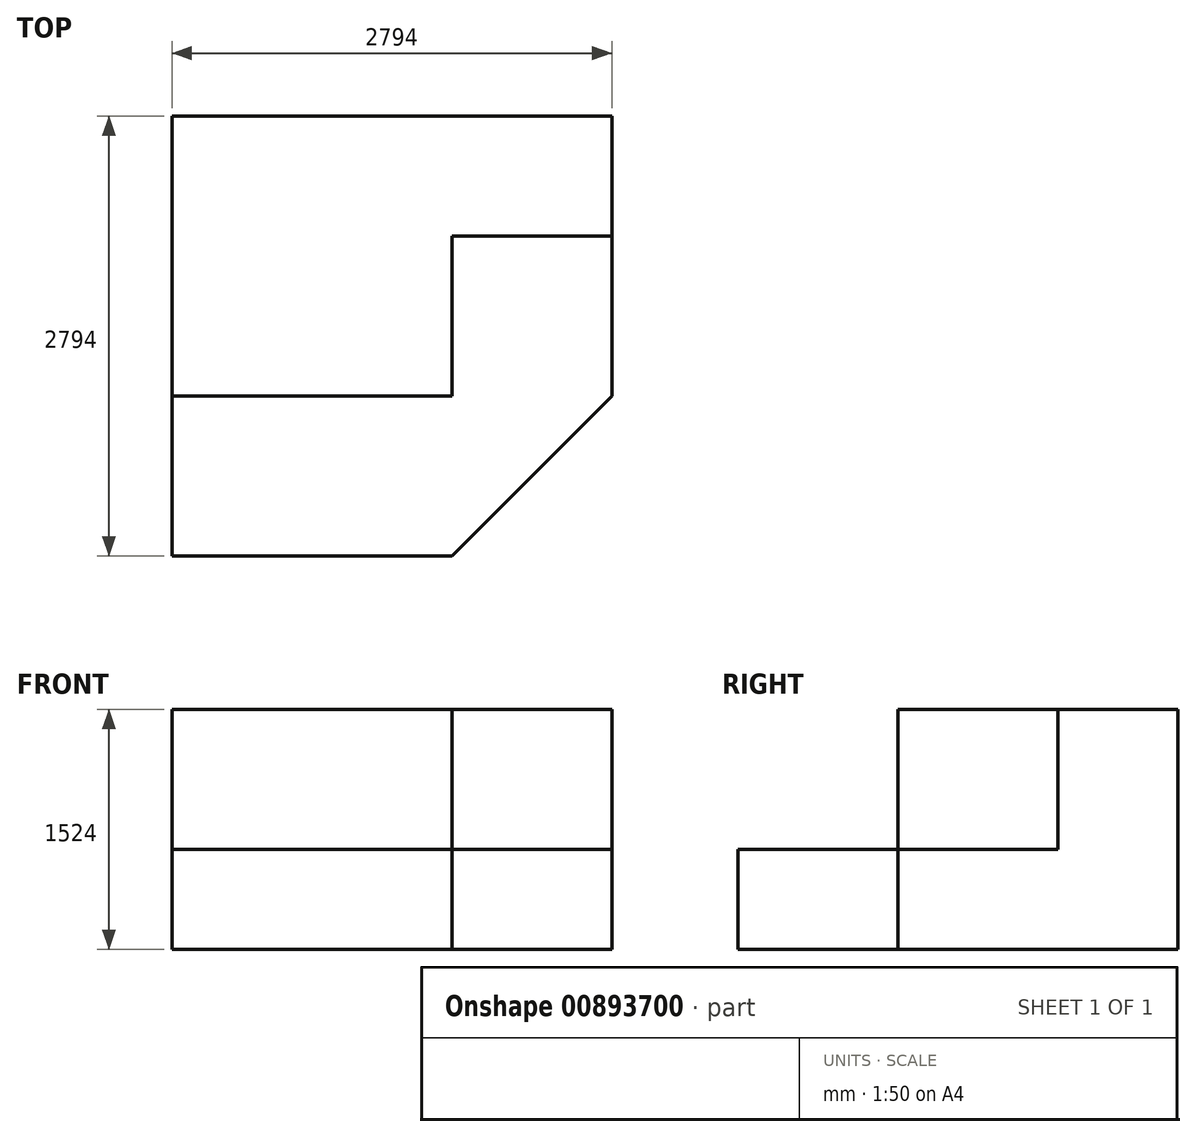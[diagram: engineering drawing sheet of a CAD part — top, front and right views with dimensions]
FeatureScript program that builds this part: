
annotation { "Feature Type Name" : "Feature", "Feature Type Description" : "" }
export const myFeature = defineFeature(function(context is Context, id is Id, definition is map)
    precondition{}
    {
        {
            var Q0;
            Q0=qCreatedBy(makeId("Top.planeOp"),FACE);
            var sketch = newSketch(context, id + "F0", { "sketchPlane" : qUnion([Q0])});
            skLineSegment(sketch, "E0", {"start": v(0, 0) * mm, "end": v(2794, 0) * mm});
            skLineSegment(sketch, "E1", {"start": v(2794, 0) * mm, "end": v(2794, 2794) * mm});
            skLineSegment(sketch, "E2", {"start": v(2794, 2794) * mm, "end": v(0, 2794) * mm});
            skLineSegment(sketch, "E3", {"start": v(0, 2794) * mm, "end": v(0, 0) * mm});
            skSolve(sketch);
        }
        {
            var Q0;
            Q0=makeQuery(id+"F0.imprint","IMPRINT",FACE,{"disambiguationData":[TD([[makeQuery(id+"F0.imprint","IMPRINT",EDGE,{"derivedFrom":sQuery(id+"F0.wireOp",EDGE,"E0")}),1.0]])]});
            extrude(context, id + "F1", {"entities" : qUnion([Q0]), "depth" : 635 * mm, "offsetDistance" : 25.4 * mm});
        }
        {
            var Q0;
            Q0=makeQuery(id+"F1.opExtrude","CAP_FACE",FACE,{"disambiguationData":[OSD([sQuery(id+"F0.wireOp",EDGE,"E0"),sQuery(id+"F0.wireOp",EDGE,"E1"),sQuery(id+"F0.wireOp",EDGE,"E2"),sQuery(id+"F0.wireOp",EDGE,"E3")])],"isStart":false});
            var sketch = newSketch(context, id + "F2", { "sketchPlane" : qUnion([Q0])});
            skLineSegment(sketch, "E4", {"start": v(0, 2794) * mm, "end": v(2794, 2794) * mm});
            skLineSegment(sketch, "E5", {"start": v(2794, 2794) * mm, "end": v(2794, 2032) * mm});
            skLineSegment(sketch, "E6", {"start": v(2794, 2032) * mm, "end": v(1778, 2032) * mm});
            skLineSegment(sketch, "E7", {"start": v(1778, 2032) * mm, "end": v(1778, 1016) * mm});
            skLineSegment(sketch, "E8", {"start": v(1778, 1016) * mm, "end": v(0, 1016) * mm});
            skLineSegment(sketch, "E9", {"start": v(0, 1016) * mm, "end": v(0, 2794) * mm});
            skSolve(sketch);
        }
        {
            var Q0;
            Q0=makeQuery(id+"F2.imprint","IMPRINT",FACE,{"disambiguationData":[TD([[makeQuery(id+"F2.imprint","IMPRINT",EDGE,{"derivedFrom":sQuery(id+"F2.wireOp",EDGE,"E4")}),1.0]])]});
            extrude(context, id + "F3", {"entities" : qUnion([Q0]), "operationType" : NewBodyOperationType.ADD, "depth" : 889 * mm, "offsetDistance" : 25.4 * mm});
        }
        {
            var Q0;
            Q0=makeQuery(id+"F1.opExtrude","CAP_FACE",FACE,{"disambiguationData":[OSD([sQuery(id+"F0.wireOp",EDGE,"E0"),sQuery(id+"F0.wireOp",EDGE,"E1"),sQuery(id+"F0.wireOp",EDGE,"E2"),sQuery(id+"F0.wireOp",EDGE,"E3")])],"isStart":false});
            var sketch = newSketch(context, id + "F4", { "sketchPlane" : qUnion([Q0])});
            skLineSegment(sketch, "E10", {"start": v(1778, 0) * mm, "end": v(2794, 1016) * mm});
            skLineSegment(sketch, "E11", {"start": v(2794, 1016) * mm, "end": v(2794, 0) * mm});
            skLineSegment(sketch, "E12", {"start": v(2794, 0) * mm, "end": v(1778, 0) * mm});
            skSolve(sketch);
        }
        {
            var Q0;
            Q0=makeQuery(id+"F4.imprint","IMPRINT",FACE,{"disambiguationData":[TD([[makeQuery(id+"F4.imprint","IMPRINT",EDGE,{"derivedFrom":sQuery(id+"F4.wireOp",EDGE,"E10")}),-1.0]])]});
            extrude(context, id + "F5", {"entities" : qUnion([Q0]), "operationType" : NewBodyOperationType.REMOVE, "oppositeDirection" : true, "depth" : 635 * mm, "offsetDistance" : 25.4 * mm});
        }
    });
